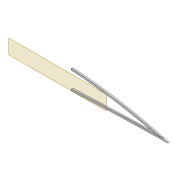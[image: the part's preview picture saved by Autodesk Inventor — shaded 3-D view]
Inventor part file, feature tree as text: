
AUTODESK INVENTOR PART (.ipt)
format: ipt  version: 2022 (Build 260153000, 153)  size: 410,624 bytes
history: native  units: mm
features: extrude x8, sketch x7, projected_geometry x6, fillet x2, shell x1, plane x1
ambient origin geometry x8: Origin, YZ Plane, XZ Plane, XY Plane, X Axis, Y Axis, Z Axis, Center Point
bodies: Solid1 (feature_tree)
feature tree (25):
  extrude  "Extrusion1"  Depth=5.0mm
  shell  "Shell1"  Thickness=2.0mm
  extrude  "Extrusion8"  Depth=5.9mm
  extrude  "Extrusion3"  Depth=10.0mm TaperAngle=0.0deg
  extrude  "Extrusion4"  Depth=2.0mm
  fillet  "Fillet1"  Radius=5.0mm
  sketch  "Sketch10"  dims[d22=4.0mm d23=0.0mm d31=2.0mm d32=5.0mm]
  extrude  "Extrusion5"  Depth=2.5mm
  plane  "Work Plane2"
  extrude  "Extrusion9"  Depth=1.6mm
  fillet  "Fillet2"  Radius=2.5mm
  extrude  "Extrusion10"  Depth=6.0mm
  extrude  "Extrusion11"  Depth=4.0mm TaperAngle=0.0deg
  sketch  "Sketch3"  dims[d0=4.0mm d1=0.0mm d2=5.0mm d7=2.0mm]
  sketch  "Sketch8"  dims[d8=2.0mm d9=5.9mm]
  sketch  "Sketch9"  dims[d13=10.0mm d14=0.0mm d16=10.0mm d17=0.0mm]
  projected_geometry  "Projected Loop4"
  projected_geometry  "Projected Loop10"
  sketch  "Sketch24"  dims[d34=1.6mm d35=2.5mm]
  projected_geometry  "Projected Loop11"
  projected_geometry  "Projected Loop12"
  projected_geometry  "Projected Loop13"
  sketch  "Sketch26"  dims[d37=5.0mm d38=1.6mm d40=2.5mm]
  projected_geometry  "Projected Loop14"
  sketch  "Sketch27"  dims[d62=80.0mm d63=6.0mm d64=4.0mm d65=0.0mm d66=3.0mm d67=12.0mm d68=5.0mm d69=15.0mm d70=12.0mm d71=3.05mm d72=10.0mm d73=0.0mm d74=2.0mm d75=100.0mm d76=20.0mm d77=0.5mm d78=10.0mm d79=0.0mm d80=10.0mm d81=0.0mm]
